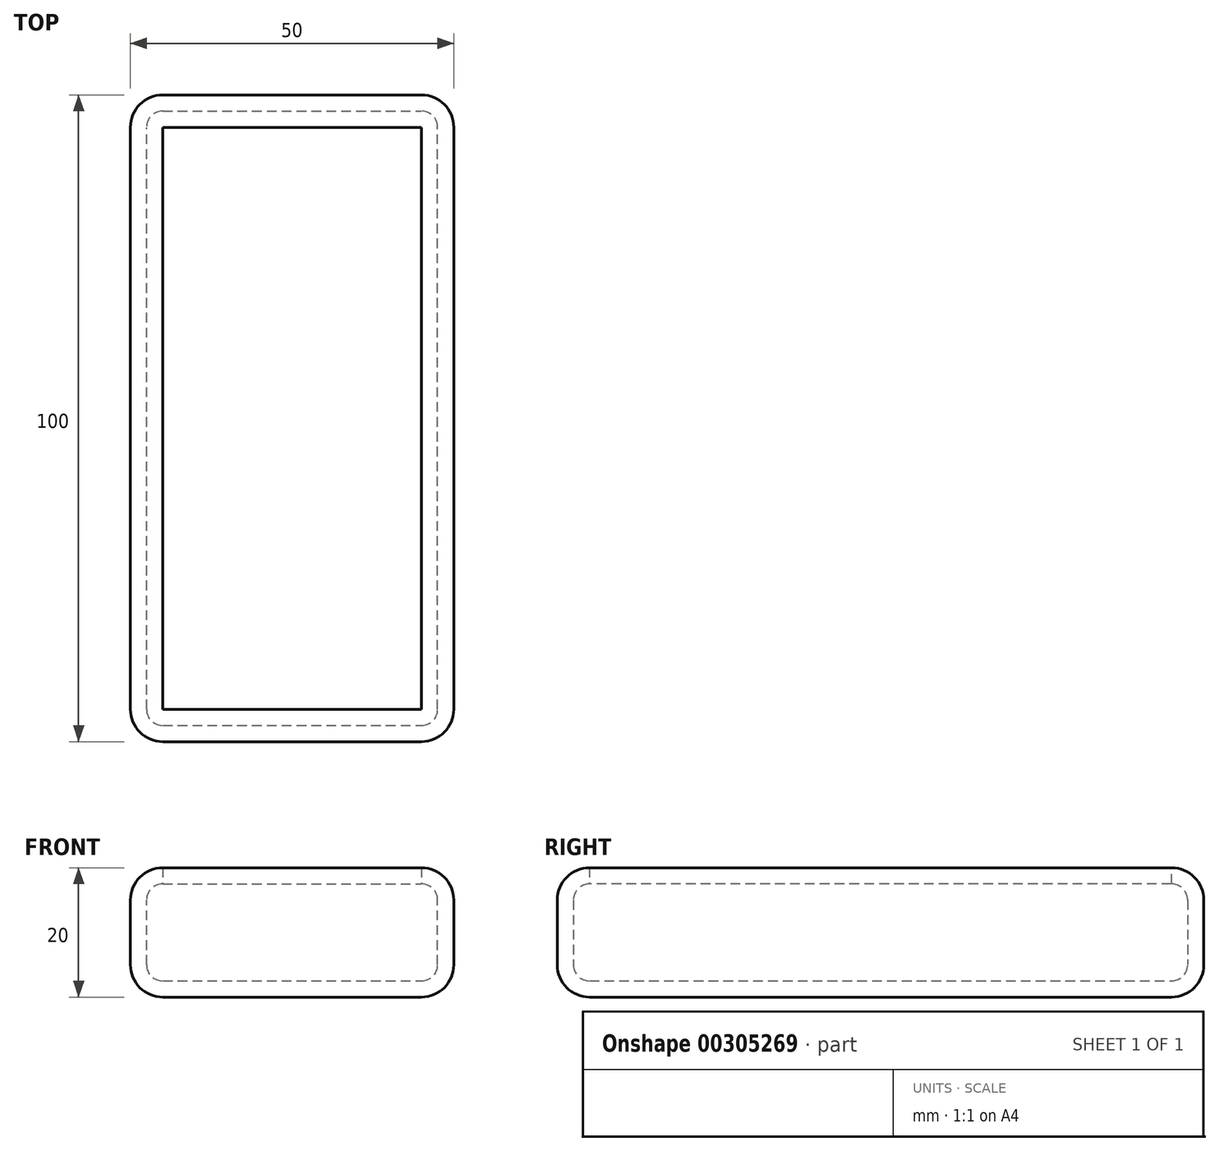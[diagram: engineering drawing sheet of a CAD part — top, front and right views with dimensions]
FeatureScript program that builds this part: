
annotation { "Feature Type Name" : "Feature", "Feature Type Description" : "" }
export const myFeature = defineFeature(function(context is Context, id is Id, definition is map)
    precondition{}
    {
        {
            var Q0;
            Q0=qCreatedBy(makeId("Right.planeOp"),FACE);
            var sketch = newSketch(context, id + "F0", { "sketchPlane" : qUnion([Q0])});
            skLineSegment(sketch, "E0.bottom", {"start": v(-50, -10) * mm, "end": v(50, -10) * mm});
            skLineSegment(sketch, "E0.top", {"start": v(-50, 10) * mm, "end": v(50, 10) * mm});
            skLineSegment(sketch, "E0.left", {"start": v(-50, -10) * mm, "end": v(-50, 10) * mm});
            skLineSegment(sketch, "E0.right", {"start": v(50, -10) * mm, "end": v(50, 10) * mm});
            skPoint(sketch, "E0.middle", {"position": v(0, 0) * mm});
            skSolve(sketch);
        }
        {
            var Q0;
            Q0 = qSketchRegion(id + "F0", true);
            extrude(context, id + "F1", {"entities" : qUnion([Q0]), "depth" : 50 * mm});
        }
        {
            var Q0;
            Q0=makeQuery(id+"F1.opExtrude","SWEPT_EDGE",EDGE,{"disambiguationData":[OSD([sQuery(id+"F0.wireOp",EDGE,"E0.bottom"),sQuery(id+"F0.wireOp",EDGE,"E0.left")])]});
            var Q1;
            Q1=makeQuery(id+"F1.opExtrude","CAP_EDGE",EDGE,{"disambiguationData":[OSD([sQuery(id+"F0.wireOp",EDGE,"E0.left")])],"isStart":false});
            var Q2;
            Q2=makeQuery(id+"F1.opExtrude","CAP_EDGE",EDGE,{"disambiguationData":[OSD([sQuery(id+"F0.wireOp",EDGE,"E0.left")])],"isStart":true});
            var Q3;
            Q3=makeQuery(id+"F1.opExtrude","CAP_EDGE",EDGE,{"disambiguationData":[OSD([sQuery(id+"F0.wireOp",EDGE,"E0.bottom")])],"isStart":true});
            var Q4;
            Q4=makeQuery(id+"F1.opExtrude","CAP_EDGE",EDGE,{"disambiguationData":[OSD([sQuery(id+"F0.wireOp",EDGE,"E0.bottom")])],"isStart":false});
            var Q5;
            Q5=makeQuery(id+"F1.opExtrude","CAP_EDGE",EDGE,{"disambiguationData":[OSD([sQuery(id+"F0.wireOp",EDGE,"E0.right")])],"isStart":false});
            var Q6;
            Q6=makeQuery(id+"F1.opExtrude","CAP_EDGE",EDGE,{"disambiguationData":[OSD([sQuery(id+"F0.wireOp",EDGE,"E0.right")])],"isStart":true});
            var Q7;
            Q7=makeQuery(id+"F1.opExtrude","SWEPT_FACE",FACE,{"disambiguationData":[OSD([sQuery(id+"F0.wireOp",EDGE,"E0.bottom")])]});
            var Q8;
            Q8=makeQuery(id+"F1.opExtrude","SWEPT_EDGE",EDGE,{"disambiguationData":[OSD([sQuery(id+"F0.wireOp",EDGE,"E0.top"),sQuery(id+"F0.wireOp",EDGE,"E0.right")])]});
            var Q9;
            Q9=makeQuery(id+"F1.opExtrude","CAP_EDGE",EDGE,{"disambiguationData":[OSD([sQuery(id+"F0.wireOp",EDGE,"E0.top")])],"isStart":true});
            var Q10;
            Q10=makeQuery(id+"F1.opExtrude","SWEPT_EDGE",EDGE,{"disambiguationData":[OSD([sQuery(id+"F0.wireOp",EDGE,"E0.top"),sQuery(id+"F0.wireOp",EDGE,"E0.left")])]});
            var Q11;
            Q11=makeQuery(id+"F1.opExtrude","CAP_EDGE",EDGE,{"disambiguationData":[OSD([sQuery(id+"F0.wireOp",EDGE,"E0.top")])],"isStart":false});
            fillet(context, id + "F2", {"entities" : qUnion([Q0, Q1, Q2, Q3, Q4, Q5, Q6, Q7, Q8, Q9, Q10, Q11]), "radius" : 5 * mm, "tangentPropagation" : true, "allowEdgeOverflow" : false});
        }
        {
            var Q0;
            Q0=makeQuery(id+"F1.opExtrude","SWEPT_FACE",FACE,{"disambiguationData":[OSD([sQuery(id+"F0.wireOp",EDGE,"E0.top")])]});
            shell(context, id + "F3", {"entities" : qUnion([Q0]), "thickness" : 2.5 * mm});
        }
    });
